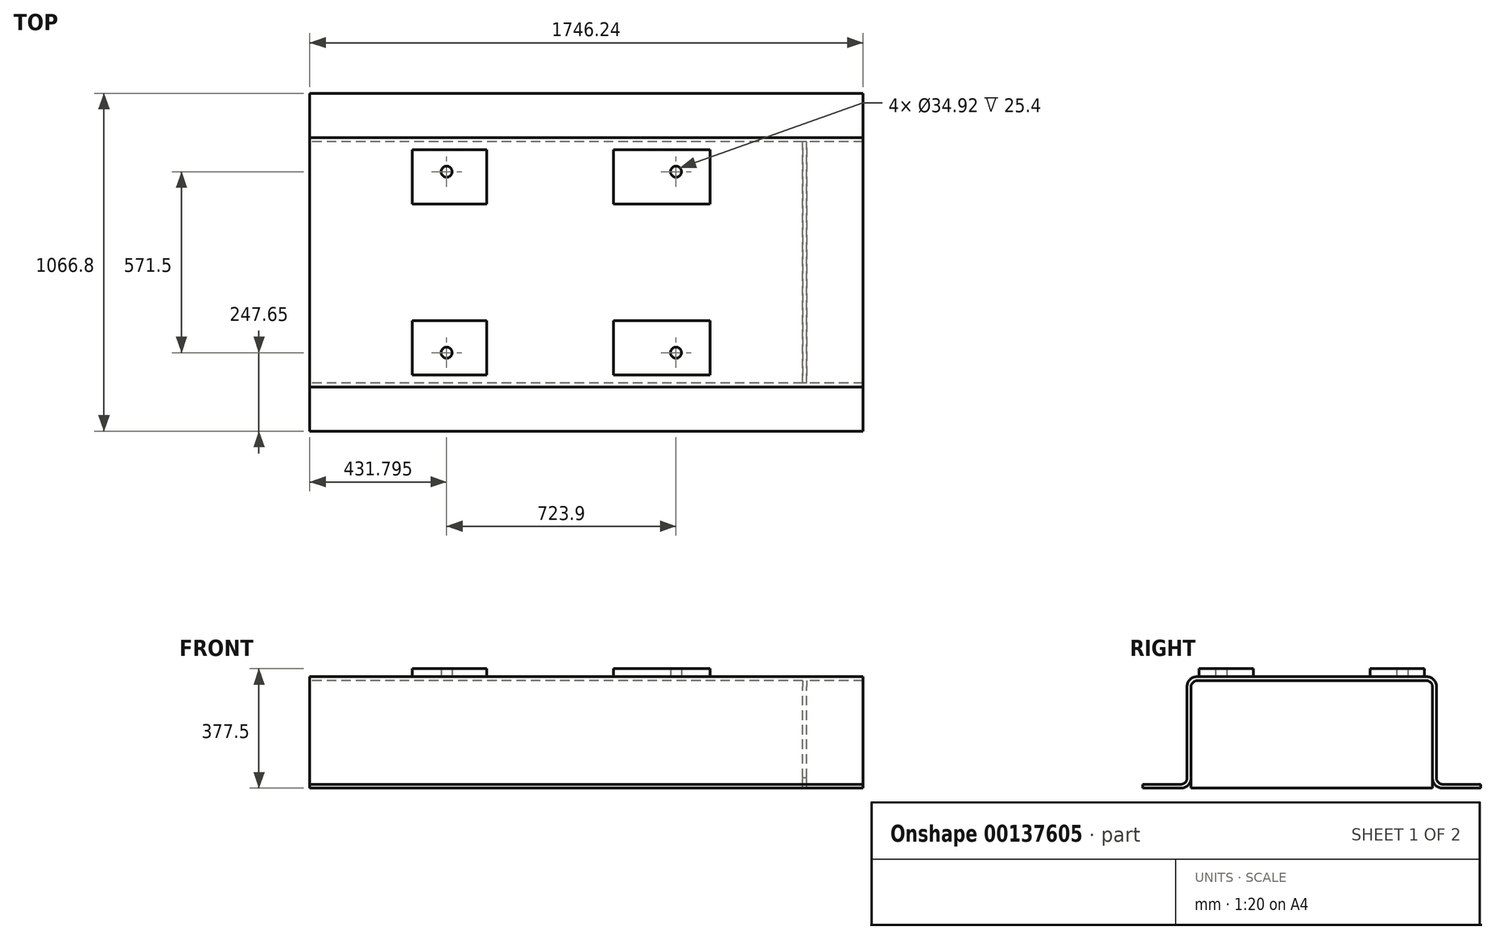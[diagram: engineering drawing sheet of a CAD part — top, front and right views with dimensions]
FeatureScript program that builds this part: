
annotation { "Feature Type Name" : "Feature", "Feature Type Description" : "" }
export const myFeature = defineFeature(function(context is Context, id is Id, definition is map)
    precondition{}
    {
        {
            var Q0;
            Q0=qCreatedBy(makeId("Right.planeOp"),FACE);
            var sketch = newSketch(context, id + "F0", { "sketchPlane" : qUnion([Q0])});
            skLineSegment(sketch, "E0", {"start": v(0, 473.15) * mm, "end": v(0, -407.2) * mm, "construction": true});
            skLineSegment(sketch, "E1.0", {"start": v(0, 352.55) * mm, "end": v(361.95, 352.55) * mm});
            skLineSegment(sketch, "E2.0", {"start": v(0, 339.85) * mm, "end": v(361.95, 339.85) * mm});
            skLineSegment(sketch, "E3.0", {"start": v(393.7, 320.8) * mm, "end": v(393.7, 31.75) * mm});
            skLineSegment(sketch, "E4.0", {"start": v(381, 320.8) * mm, "end": v(381, 32.2) * mm});
            skLineSegment(sketch, "E5.trimOffspring", {"start": v(412.75, 12.7) * mm, "end": v(520.7, 12.7) * mm});
            skLineSegment(sketch, "E6.trimOffspring", {"start": v(412.75, 0.45) * mm, "end": v(533.4, 0.45) * mm});
            skPoint(sketch, "E7.start.orphan", {"position": v(-520.7, 0) * mm});
            skArc(sketch, "E8.filletArc", {"start": v(381, 320.8) * mm, "mid": v(375.42, 334.27) * mm, "end": v(361.95, 339.85) * mm});
            skArc(sketch, "E9.filletArc", {"start": v(393.7, 31.75) * mm, "mid": v(399.28, 18.28) * mm, "end": v(412.75, 12.7) * mm});
            skArc(sketch, "E10.filletArc", {"start": v(381, 32.2) * mm, "mid": v(390.3, 9.75) * mm, "end": v(412.75, 0.45) * mm});
            skArc(sketch, "E11.filletArc", {"start": v(393.7, 320.8) * mm, "mid": v(384.4, 343.25) * mm, "end": v(361.95, 352.55) * mm});
            skLineSegment(sketch, "E12", {"start": v(0, 0) * mm, "end": v(739.32, 0) * mm, "construction": true});
            skLineSegment(sketch, "E13", {"start": v(533.4, 0.45) * mm, "end": v(533.4, 12.7) * mm});
            skLineSegment(sketch, "E14", {"start": v(533.4, 12.7) * mm, "end": v(516.63, 12.7) * mm});
            skLineSegment(sketch, "E15", {"start": v(0, 352.55) * mm, "end": v(0, 339.85) * mm});
            skArc(sketch, "E16.MirrorCS", {"start": v(-381, 320.8) * mm, "mid": v(-375.42, 334.27) * mm, "end": v(-361.95, 339.85) * mm});
            skArc(sketch, "E17.MirrorCS", {"start": v(-393.7, 31.75) * mm, "mid": v(-399.28, 18.28) * mm, "end": v(-412.75, 12.7) * mm});
            skArc(sketch, "E18.MirrorCS", {"start": v(-381, 32.2) * mm, "mid": v(-390.3, 9.75) * mm, "end": v(-412.75, 0.45) * mm});
            skLineSegment(sketch, "E19.MirrorCS", {"start": v(-533.4, 0.45) * mm, "end": v(-533.4, 12.7) * mm});
            skLineSegment(sketch, "E20.MirrorCS", {"start": v(-533.4, 12.7) * mm, "end": v(-516.63, 12.7) * mm});
            skArc(sketch, "E21.MirrorCS", {"start": v(-393.7, 320.8) * mm, "mid": v(-384.4, 343.25) * mm, "end": v(-361.95, 352.55) * mm});
            skLineSegment(sketch, "E22.MirrorCS", {"start": v(-412.75, 0.45) * mm, "end": v(-533.4, 0.45) * mm});
            skLineSegment(sketch, "E23.MirrorCS", {"start": v(-412.75, 12.7) * mm, "end": v(-520.7, 12.7) * mm});
            skLineSegment(sketch, "E24.MirrorCS", {"start": v(-381, 320.8) * mm, "end": v(-381, 32.2) * mm});
            skLineSegment(sketch, "E25.MirrorCS", {"start": v(0, 0) * mm, "end": v(-739.32, 0) * mm, "construction": true});
            skLineSegment(sketch, "E26.MirrorCS", {"start": v(0, 352.55) * mm, "end": v(-361.95, 352.55) * mm});
            skLineSegment(sketch, "E27.MirrorCS", {"start": v(-393.7, 320.8) * mm, "end": v(-393.7, 31.75) * mm});
            skLineSegment(sketch, "E28.MirrorCS", {"start": v(0, 339.85) * mm, "end": v(-361.95, 339.85) * mm});
            skSolve(sketch);
        }
        {
            var Q0;
            Q0=makeQuery(id+"F0.imprint","IMPRINT",FACE,{"disambiguationData":[TD([[makeQuery(id+"F0.imprint","IMPRINT",EDGE,{"derivedFrom":sQuery(id+"F0.wireOp",EDGE,"E15")}),-1.0]])]});
            var Q1;
            Q1=makeQuery(id+"F0.imprint","IMPRINT",FACE,{"disambiguationData":[TD([[makeQuery(id+"F0.imprint","IMPRINT",EDGE,{"derivedFrom":sQuery(id+"F0.wireOp",EDGE,"E1.0")}),-1.0]])]});
            extrude(context, id + "F1", {"entities" : qUnion([Q0, Q1]), "endBound" : BoundingType.SYMMETRIC, "depth" : 1746.25 * mm});
        }
        {
            var Q0;
            Q0=makeQuery(id+"F1.opExtrude","SWEPT_FACE",FACE,{"disambiguationData":[OSD([sQuery(id+"F0.wireOp",EDGE,"E2.0"),sQuery(id+"F0.wireOp",EDGE,"E28.MirrorCS")])]});
            var sketch = newSketch(context, id + "F2", { "sketchPlane" : qUnion([Q0])});
            skLineSegment(sketch, "E29.0", {"start": v(695.32, -381) * mm, "end": v(695.32, 381) * mm});
            skLineSegment(sketch, "E30.0", {"start": v(682.62, -381) * mm, "end": v(682.62, 381) * mm});
            skLineSegment(sketch, "E31.0", {"start": v(695.32, 381) * mm, "end": v(682.62, 381) * mm});
            skLineSegment(sketch, "E32.0", {"start": v(695.32, -381) * mm, "end": v(682.62, -381) * mm});
            skPoint(sketch, "E33.orphan", {"position": v(-873.12, 381) * mm});
            skPoint(sketch, "E34.orphan", {"position": v(873.12, 381) * mm});
            skPoint(sketch, "E35.orphan", {"position": v(-873.12, -381) * mm});
            skPoint(sketch, "E36.orphan", {"position": v(873.12, -381) * mm});
            skSolve(sketch);
        }
        {
            var Q0;
            Q0=qSketchRegion(id+"F2",true);
            var Q1;
            Q1=makeQuery(id+"F1.opExtrude","SWEPT_FACE",FACE,{"disambiguationData":[OSD([sQuery(id+"F0.wireOp",EDGE,"E6.trimOffspring")])]});
            extrude(context, id + "F3", {"entities" : qUnion([Q0]), "operationType" : NewBodyOperationType.ADD, "endBound" : BoundingType.UP_TO_SURFACE, "endBoundEntityFace" : qUnion([Q1]), "depth" : 25.4 * mm});
        }
        {
            var Q0;
            Q0=makeQuery(id+"F1.opExtrude","SWEPT_FACE",FACE,{"disambiguationData":[OSD([sQuery(id+"F0.wireOp",EDGE,"E1.0"),sQuery(id+"F0.wireOp",EDGE,"E26.MirrorCS")])]});
            var sketch = newSketch(context, id + "F4", { "sketchPlane" : qUnion([Q0])});
            skLineSegment(sketch, "E37.0", {"start": v(-1673.23, 361.95) * mm, "end": v(-1673.23, -1102.1) * mm, "construction": true});
            skLineSegment(sketch, "E38.0", {"start": v(-1209.68, 361.95) * mm, "end": v(-1209.68, -1102.1) * mm, "construction": true});
            skLineSegment(sketch, "E39.0", {"start": v(-79.38, 361.95) * mm, "end": v(-79.38, -1102.1) * mm, "construction": true});
            skLineSegment(sketch, "E40.0", {"start": v(644.52, 361.95) * mm, "end": v(644.52, -1102.1) * mm, "construction": true});
            skLineSegment(sketch, "E41", {"start": v(-1510, 0) * mm, "end": v(1125.96, 0) * mm, "construction": true});
            skPoint(sketch, "E41.endSnap0", {"position": v(873.12, 0) * mm});
            skLineSegment(sketch, "E42.0", {"start": v(85.72, 361.95) * mm, "end": v(85.72, -1102.1) * mm, "construction": true});
            skLineSegment(sketch, "E43.0", {"start": v(390.52, 361.95) * mm, "end": v(390.52, -1102.1) * mm, "construction": true});
            skLineSegment(sketch, "E44.0", {"start": v(-314.33, 361.95) * mm, "end": v(-314.33, -1102.1) * mm, "construction": true});
            skLineSegment(sketch, "E45.0", {"start": v(-549.28, 361.95) * mm, "end": v(-549.28, -1102.1) * mm, "construction": true});
            skLineSegment(sketch, "E46.0", {"start": v(-1510, 184.15) * mm, "end": v(1125.96, 184.15) * mm, "construction": true});
            skLineSegment(sketch, "E47.0", {"start": v(-1510, 355.6) * mm, "end": v(1125.96, 355.6) * mm, "construction": true});
            skLineSegment(sketch, "E48.bottom", {"start": v(-549.28, 355.6) * mm, "end": v(-314.33, 355.6) * mm});
            skLineSegment(sketch, "E48.top", {"start": v(-549.28, 184.15) * mm, "end": v(-314.33, 184.15) * mm});
            skLineSegment(sketch, "E48.left", {"start": v(-549.28, 355.6) * mm, "end": v(-549.28, 184.15) * mm});
            skLineSegment(sketch, "E48.right", {"start": v(-314.33, 355.6) * mm, "end": v(-314.33, 184.15) * mm});
            skLineSegment(sketch, "E49.bottom", {"start": v(390.52, 355.6) * mm, "end": v(85.72, 355.6) * mm});
            skLineSegment(sketch, "E49.top", {"start": v(390.52, 184.15) * mm, "end": v(85.72, 184.15) * mm});
            skLineSegment(sketch, "E49.left", {"start": v(390.52, 355.6) * mm, "end": v(390.52, 184.15) * mm});
            skLineSegment(sketch, "E49.right", {"start": v(85.72, 355.6) * mm, "end": v(85.72, 184.15) * mm});
            skLineSegment(sketch, "E50.0", {"start": v(-1510, 285.75) * mm, "end": v(1125.96, 285.75) * mm, "construction": true});
            skLineSegment(sketch, "E51.0", {"start": v(-441.33, 361.95) * mm, "end": v(-441.33, -1102.1) * mm, "construction": true});
            skLineSegment(sketch, "E52.0", {"start": v(282.57, 361.95) * mm, "end": v(282.57, -1102.1) * mm, "construction": true});
            skCircle(sketch, "E53", {"center": v(-441.33, 285.75) * mm, "radius": 17.46 * mm});
            skCircle(sketch, "E54", {"center": v(282.57, 285.75) * mm, "radius": 17.46 * mm});
            skLineSegment(sketch, "E55.MirrorCS", {"start": v(390.52, -184.15) * mm, "end": v(85.72, -184.15) * mm});
            skLineSegment(sketch, "E56.MirrorCS", {"start": v(390.52, -355.6) * mm, "end": v(390.52, -184.15) * mm});
            skCircle(sketch, "E57.MirrorC", {"center": v(-441.33, -285.75) * mm, "radius": 17.46 * mm});
            skLineSegment(sketch, "E58.MirrorCS", {"start": v(85.72, -355.6) * mm, "end": v(85.72, -184.15) * mm});
            skLineSegment(sketch, "E59.MirrorCS", {"start": v(-549.28, -355.6) * mm, "end": v(-549.28, -184.15) * mm});
            skCircle(sketch, "E60.MirrorC", {"center": v(282.57, -285.75) * mm, "radius": 17.46 * mm});
            skLineSegment(sketch, "E61.MirrorCS", {"start": v(390.52, -355.6) * mm, "end": v(85.72, -355.6) * mm});
            skLineSegment(sketch, "E62.MirrorCS", {"start": v(-314.33, -355.6) * mm, "end": v(-314.33, -184.15) * mm});
            skLineSegment(sketch, "E63.MirrorCS", {"start": v(-549.28, -355.6) * mm, "end": v(-314.33, -355.6) * mm});
            skLineSegment(sketch, "E64.MirrorCS", {"start": v(-549.28, -184.15) * mm, "end": v(-314.33, -184.15) * mm});
            skSolve(sketch);
        }
        {
            var Q0;
            Q0=qSketchRegion(id+"F4",true);
            extrude(context, id + "F5", {"entities" : qUnion([Q0]), "operationType" : NewBodyOperationType.ADD, "depth" : 25.4 * mm});
        }
    });
